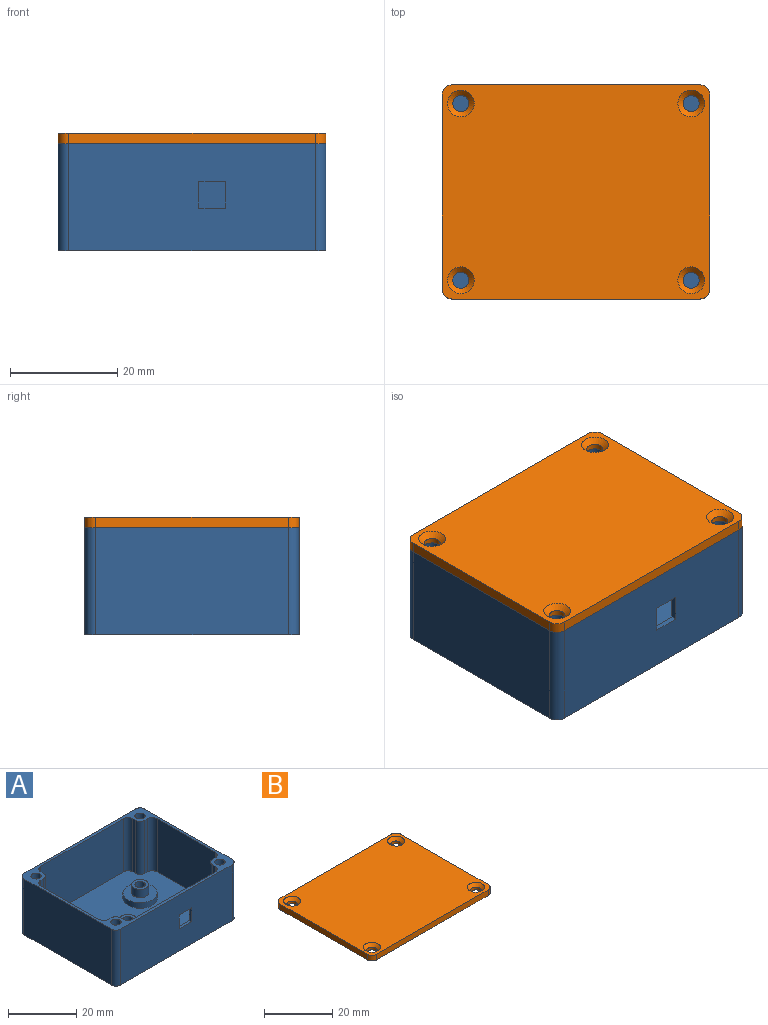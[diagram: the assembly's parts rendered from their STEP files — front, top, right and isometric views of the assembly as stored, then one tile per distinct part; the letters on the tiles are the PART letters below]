
ASSEMBLY  parts=2 mates=1
PART A: 71 faces, bbox 50x40x20 mm
  f0: plane 34x19mm, normal (0,1,0), area 621mm2, adj f4,f8,f55,f59,f67,f68,f69,f70
  f1: plane 46x20mm, normal (0,-1,0), area 895mm2, adj f8,f12,f52,f53,f67,f68,f69,f70
  f2: cylinder r=1.5mm len=4mm, axis (0,0,-1), area 37.7mm2, adj f30,f50
  f3: cylinder r=1.5mm len=4mm, axis (0,0,-1), area 37.7mm2, adj f32,f43
  f4: plane 48x38mm, normal (0,0,1), area 1563.5mm2, adj f0,f5,f6,f7,f13,f14,f15,f16
  f5: plane 24x19mm, normal (-1,0,0), area 456mm2, adj f4,f8,f57,f61
  f6: plane 24x19mm, normal (1,0,0), area 456mm2, adj f4,f8,f60,f66
  f7: plane 34x19mm, normal (0,-1,0), area 646mm2, adj f4,f8,f62,f64
  f8: plane 50x40mm, normal (0,0,1), area 247.7mm2, adj f0,f1,f5,f6,f7,f9,f10,f11
  f9: plane 46x20mm, normal (0,1,0), area 920mm2, adj f8,f12,f51,f54
  f10: plane 36x20mm, normal (-1,0,0), area 720mm2, adj f8,f12,f51,f52
  f11: plane 36x20mm, normal (1,0,0), area 720mm2, adj f8,f12,f53,f54
  f12: plane 50x40mm, normal (0,0,-1), area 1949.8mm2, adj f1,f9,f10,f11,f37,f38,f39,f40
  f13: plane 19x1mm, normal (0,-1,0), area 19mm2, adj f4,f8,f65,f66
  f14: plane 19x1mm, normal (1,0,0), area 19mm2, adj f4,f8,f64,f65
  f15: plane 19x1mm, normal (0,-1,0), area 19mm2, adj f4,f8,f61,f63
  f16: plane 19x1mm, normal (-1,0,0), area 19mm2, adj f4,f8,f62,f63
  f17: plane 19x1mm, normal (0,1,0), area 19mm2, adj f4,f8,f58,f60
  f18: plane 19x1mm, normal (1,0,0), area 19mm2, adj f4,f8,f58,f59
  f19: plane 19x1mm, normal (0,1,0), area 19mm2, adj f4,f8,f56,f57
  f20: plane 19x1mm, normal (-1,0,0), area 19mm2, adj f4,f8,f55,f56
  f21: cylinder r=1.5mm len=10mm, axis (0,0,1), area 94.2mm2, adj f8,f22
  f22: plane 3x3mm, normal (0,0,1), area 7.1mm2, adj f21
  f23: cylinder r=1.5mm len=10mm, axis (0,0,1), area 94.2mm2, adj f8,f24
  f24: plane 3x3mm, normal (0,0,1), area 7.1mm2, adj f23
  f25: cylinder r=1.5mm len=10mm, axis (0,0,1), area 94.2mm2, adj f8,f26
  f26: plane 3x3mm, normal (0,0,1), area 7.1mm2, adj f25
  f27: cylinder r=1.5mm len=10mm, axis (0,0,1), area 94.2mm2, adj f8,f28
  f28: plane 3x3mm, normal (0,0,1), area 7.1mm2, adj f27
  f29: cylinder r=2.5mm len=5mm, axis (0,0,-1), area 47.1mm2, adj f30,f34
  f30: plane 5x5mm, normal (0,0,1), area 12.6mm2, adj f2,f29
  f31: cylinder r=2.5mm len=5mm, axis (0,0,-1), area 47.1mm2, adj f32,f36
  f32: plane 5x5mm, normal (0,0,1), area 12.6mm2, adj f3,f31
  f33: cylinder r=5mm len=10mm, axis (0,0,-1), area 62.8mm2, adj f4,f34
  f34: plane 10x10mm, normal (0,0,1), area 58.9mm2, adj f29,f33
  f35: cylinder r=5mm len=10mm, axis (0,0,-1), area 62.8mm2, adj f4,f36
  f36: plane 10x10mm, normal (0,0,1), area 58.9mm2, adj f31,f35
  f37: plane 3x2mm, normal (1,0,0), area 6mm2, adj f12,f38,f42,f43
  f38: plane 2.6x2mm, normal (0.5,-0.87,0), area 6mm2, adj f12,f37,f39,f43
  f39: plane 2.6x2mm, normal (-0.5,-0.87,0), area 6mm2, adj f12,f38,f40,f43
  f40: plane 3x2mm, normal (-1,0,0), area 6mm2, adj f12,f39,f41,f43
  f41: plane 2.6x2mm, normal (-0.5,0.87,0), area 6mm2, adj f12,f40,f42,f43
  f42: plane 2.6x2mm, normal (0.5,0.87,0), area 6mm2, adj f12,f37,f41,f43
  f43: plane 6x5.2mm, normal (0,0,-1), area 16.3mm2, adj f3,f37,f38,f39,f40,f41,f42
  f44: plane 3x2mm, normal (1,0,0), area 6mm2, adj f12,f45,f49,f50
  f45: plane 2.6x2mm, normal (0.5,-0.87,0), area 6mm2, adj f12,f44,f46,f50
  f46: plane 2.6x2mm, normal (-0.5,-0.87,0), area 6mm2, adj f12,f45,f47,f50
  f47: plane 3x2mm, normal (-1,0,0), area 6mm2, adj f12,f46,f48,f50
  f48: plane 2.6x2mm, normal (-0.5,0.87,0), area 6mm2, adj f12,f47,f49,f50
  f49: plane 2.6x2mm, normal (0.5,0.87,0), area 6mm2, adj f12,f44,f48,f50
  f50: plane 6x5.2mm, normal (0,0,-1), area 16.3mm2, adj f2,f44,f45,f46,f47,f48,f49
  f51: cylinder r=2mm len=20mm, axis (0,0,1), area 62.8mm2, adj f8,f9,f10,f12
  f52: cylinder r=2mm len=20mm, axis (0,0,-1), area 62.8mm2, adj f1,f8,f10,f12
  f53: cylinder r=2mm len=20mm, axis (0,0,1), area 62.8mm2, adj f1,f8,f11,f12
  f54: cylinder r=2mm len=20mm, axis (0,0,-1), area 62.8mm2, adj f8,f9,f11,f12
  f55: cylinder r=2mm len=19mm, axis (0,0,1), area 59.7mm2, adj f0,f4,f8,f20
  f56: cylinder r=2mm len=19mm, axis (0,0,1), area 59.7mm2, adj f4,f8,f19,f20
  f57: cylinder r=2mm len=19mm, axis (0,0,1), area 59.7mm2, adj f4,f5,f8,f19
  f58: cylinder r=2mm len=19mm, axis (0,0,1), area 59.7mm2, adj f4,f8,f17,f18
  f59: cylinder r=2mm len=19mm, axis (0,0,-1), area 59.7mm2, adj f0,f4,f8,f18
  f60: cylinder r=2mm len=19mm, axis (0,0,1), area 59.7mm2, adj f4,f6,f8,f17
  f61: cylinder r=2mm len=19mm, axis (0,0,-1), area 59.7mm2, adj f4,f5,f8,f15
  f62: cylinder r=2mm len=19mm, axis (0,0,1), area 59.7mm2, adj f4,f7,f8,f16
  f63: cylinder r=2mm len=19mm, axis (0,0,1), area 59.7mm2, adj f4,f8,f15,f16
  f64: cylinder r=2mm len=19mm, axis (0,0,-1), area 59.7mm2, adj f4,f7,f8,f14
  f65: cylinder r=2mm len=19mm, axis (0,0,1), area 59.7mm2, adj f4,f8,f13,f14
  f66: cylinder r=2mm len=19mm, axis (0,0,-1), area 59.7mm2, adj f4,f6,f8,f13
  f67: plane 5x1mm, normal (0,0,-1), area 5mm2, adj f0,f1,f68,f70
  f68: plane 5x1mm, normal (1,0,0), area 5mm2, adj f0,f1,f67,f69
  f69: plane 5x1mm, normal (0,0,1), area 5mm2, adj f0,f1,f68,f70
  f70: plane 5x1mm, normal (-1,0,0), area 5mm2, adj f0,f1,f67,f69
PART B: 18 faces, bbox 50x40x2 mm
  f0: plane 46x2mm, normal (0,1,0), area 92mm2, adj f4,f5,f14,f17
  f1: plane 36x2mm, normal (-1,0,0), area 72mm2, adj f4,f5,f14,f15
  f2: plane 46x2mm, normal (0,-1,0), area 92mm2, adj f4,f5,f15,f16
  f3: plane 36x2mm, normal (1,0,0), area 72mm2, adj f4,f5,f16,f17
  f4: plane 50x40mm, normal (0,0,1), area 1918mm2, adj f0,f1,f2,f3,f10,f11,f12,f13
  f5: plane 50x40mm, normal (0,0,-1), area 1968.3mm2, adj f0,f1,f2,f3,f6,f7,f8,f9
  f6: cylinder r=1.5mm len=3mm, axis (0,0,1), area 9.4mm2, adj f5,f13
  f7: cylinder r=1.5mm len=3mm, axis (0,0,1), area 9.4mm2, adj f5,f11
  f8: cylinder r=1.5mm len=3mm, axis (0,0,1), area 9.4mm2, adj f5,f10
  f9: cylinder r=1.5mm len=3mm, axis (0,0,1), area 9.4mm2, adj f5,f12
  f10: cone r=1.5mm half-angle=45deg, axis (0,0,1), area 17.8mm2, adj f4,f8
  f11: cone r=1.5mm half-angle=45deg, axis (0,0,1), area 17.8mm2, adj f4,f7
  f12: cone r=1.5mm half-angle=45deg, axis (0,0,1), area 17.8mm2, adj f4,f9
  f13: cone r=1.5mm half-angle=45deg, axis (0,0,1), area 17.8mm2, adj f4,f6
  f14: cylinder r=2mm len=2mm, axis (0,0,1), area 6.3mm2, adj f0,f1,f4,f5
  f15: cylinder r=2mm len=2mm, axis (0,0,-1), area 6.3mm2, adj f1,f2,f4,f5
  f16: cylinder r=2mm len=2mm, axis (0,0,1), area 6.3mm2, adj f2,f3,f4,f5
  f17: cylinder r=2mm len=2mm, axis (0,0,-1), area 6.3mm2, adj f0,f3,f4,f5
PLACE A t=(-38.89,14.77,-3.85)mm fixed
PLACE B t=(-114.36,16.98,16.15)mm
MATE slider A.f25 <-> B.f7  axis (0,0,1) through (-60.26,34.5,16.15)mm
